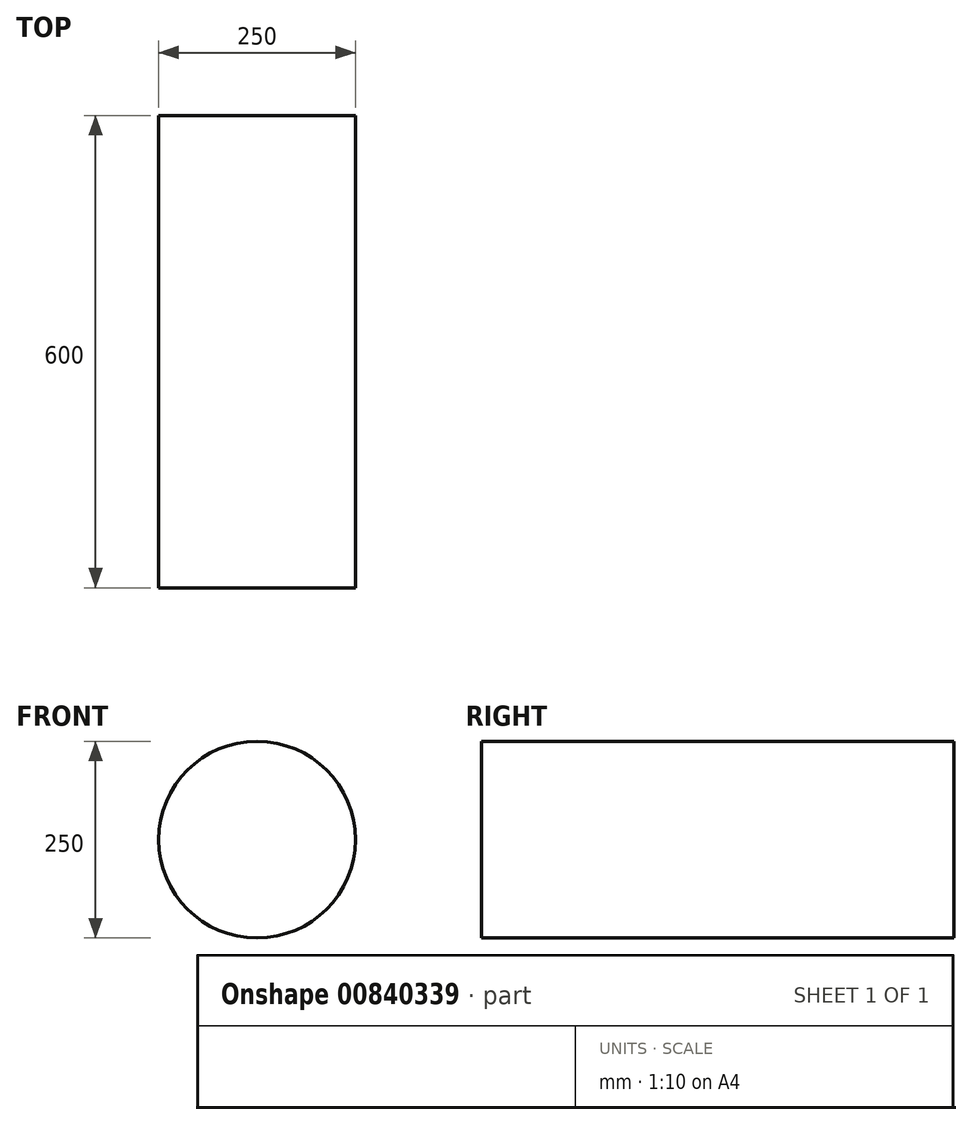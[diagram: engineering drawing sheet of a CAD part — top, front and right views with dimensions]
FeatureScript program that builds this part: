
annotation { "Feature Type Name" : "Feature", "Feature Type Description" : "" }
export const myFeature = defineFeature(function(context is Context, id is Id, definition is map)
    precondition{}
    {
        {
            var Q0;
            Q0=qCreatedBy(makeId("Front.planeOp"),FACE);
            var sketch = newSketch(context, id + "F0", { "sketchPlane" : qUnion([Q0])});
            skCircle(sketch, "E0", {"center": v(0, 0) * mm, "radius": 125 * mm});
            skSolve(sketch);
        }
        {
            var Q0;
            Q0=makeQuery(id+"F0.imprint","IMPRINT",FACE,{"disambiguationData":[TD([[makeQuery(id+"F0.imprint","IMPRINT",EDGE,{"derivedFrom":sQuery(id+"F0.wireOp",EDGE,"E0")}),1.0]])]});
            extrude(context, id + "F1", {"entities" : qUnion([Q0]), "endBound" : BoundingType.SYMMETRIC, "depth" : 600 * mm, "offsetDistance" : 25 * mm});
        }
    });
